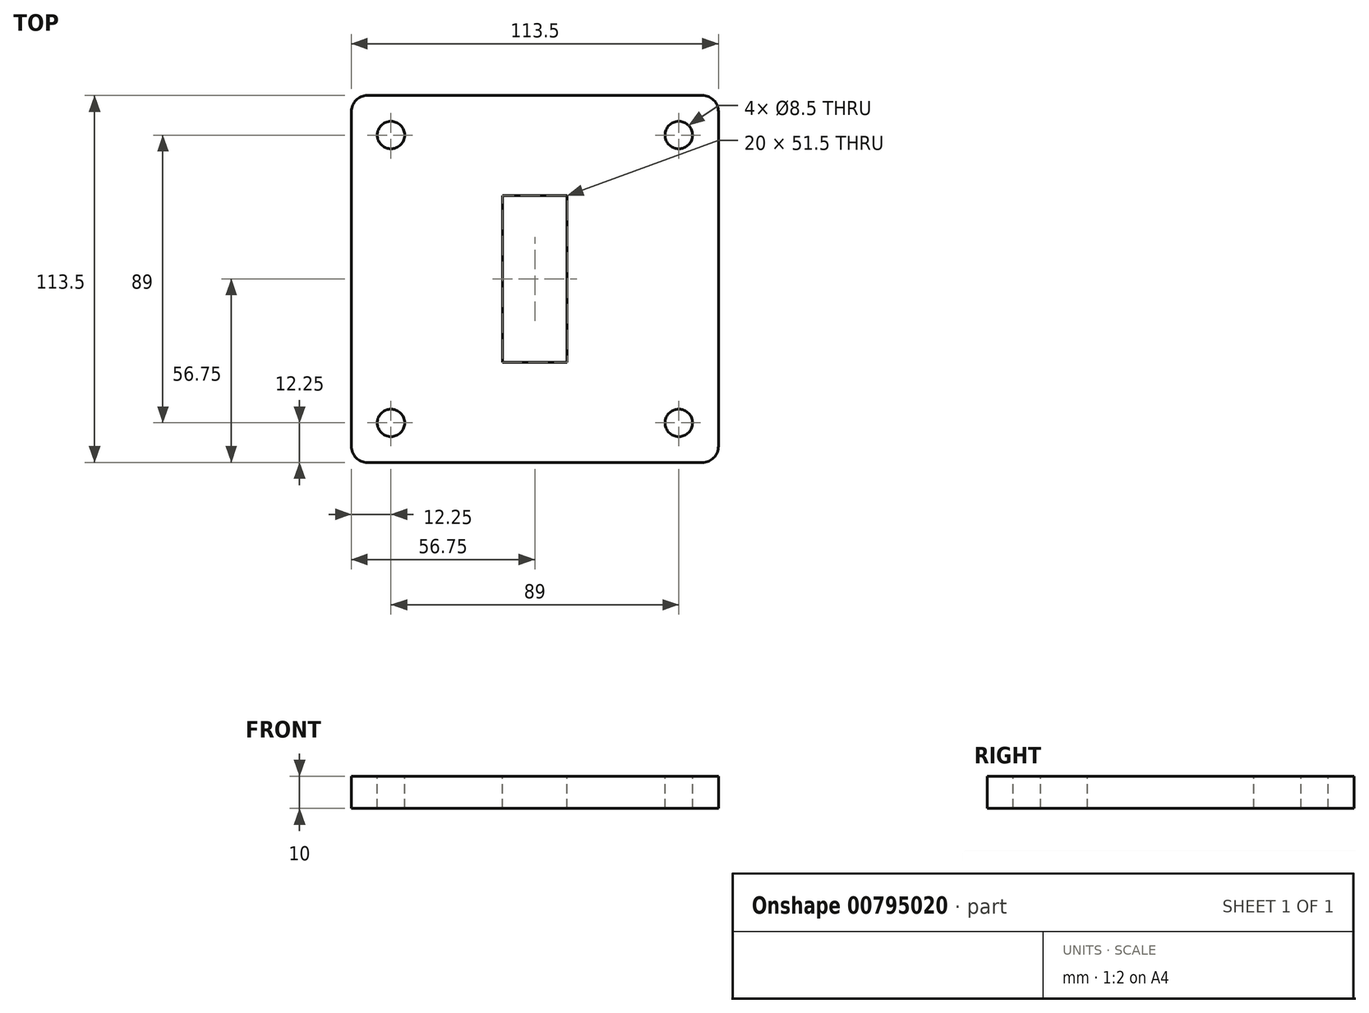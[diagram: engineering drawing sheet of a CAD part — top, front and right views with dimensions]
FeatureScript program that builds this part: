
annotation { "Feature Type Name" : "Feature", "Feature Type Description" : "" }
export const myFeature = defineFeature(function(context is Context, id is Id, definition is map)
    precondition{}
    {
        {
            var Q0;
            Q0=qCreatedBy(makeId("Top.planeOp"),FACE);
            var sketch = newSketch(context, id + "F0", { "sketchPlane" : qUnion([Q0])});
            skLineSegment(sketch, "E0.bottom", {"start": v(-56.75, 56.75) * mm, "end": v(56.75, 56.75) * mm});
            skLineSegment(sketch, "E0.top", {"start": v(-56.75, -56.75) * mm, "end": v(56.75, -56.75) * mm});
            skLineSegment(sketch, "E0.left", {"start": v(-56.75, 56.75) * mm, "end": v(-56.75, -56.75) * mm});
            skLineSegment(sketch, "E0.right", {"start": v(56.75, 56.75) * mm, "end": v(56.75, -56.75) * mm});
            skPoint(sketch, "E0.middle", {"position": v(0, 0) * mm});
            skSolve(sketch);
        }
        {
            var Q0;
            Q0=makeQuery(id+"F0.imprint","IMPRINT",FACE,{"disambiguationData":[TD([[makeQuery(id+"F0.imprint","IMPRINT",EDGE,{"derivedFrom":sQuery(id+"F0.wireOp",EDGE,"E0.bottom")}),-1.0]])]});
            extrude(context, id + "F1", {"entities" : qUnion([Q0]), "depth" : 10 * mm, "offsetDistance" : 25 * mm});
        }
        {
            var Q0;
            Q0=makeQuery(id+"F1.opExtrude","SWEPT_EDGE",EDGE,{"disambiguationData":[OSD([sQuery(id+"F0.wireOp",EDGE,"E0.top"),sQuery(id+"F0.wireOp",EDGE,"E0.left")])]});
            var Q1;
            Q1=makeQuery(id+"F1.opExtrude","SWEPT_EDGE",EDGE,{"disambiguationData":[OSD([sQuery(id+"F0.wireOp",EDGE,"E0.bottom"),sQuery(id+"F0.wireOp",EDGE,"E0.left")])]});
            var Q2;
            Q2=makeQuery(id+"F1.opExtrude","SWEPT_EDGE",EDGE,{"disambiguationData":[OSD([sQuery(id+"F0.wireOp",EDGE,"E0.bottom"),sQuery(id+"F0.wireOp",EDGE,"E0.right")])]});
            var Q3;
            Q3=makeQuery(id+"F1.opExtrude","SWEPT_EDGE",EDGE,{"disambiguationData":[OSD([sQuery(id+"F0.wireOp",EDGE,"E0.top"),sQuery(id+"F0.wireOp",EDGE,"E0.right")])]});
            fillet(context, id + "F2", {"entities" : qUnion([Q0, Q1, Q2, Q3]), "radius" : 5 * mm, "tangentPropagation" : true, "allowEdgeOverflow" : false});
        }
        {
            var Q0;
            Q0=makeQuery(id+"F1.opExtrude","CAP_FACE",FACE,{"disambiguationData":[OSD([sQuery(id+"F0.wireOp",EDGE,"E0.bottom"),sQuery(id+"F0.wireOp",EDGE,"E0.top"),sQuery(id+"F0.wireOp",EDGE,"E0.left"),sQuery(id+"F0.wireOp",EDGE,"E0.right")])],"isStart":false});
            var sketch = newSketch(context, id + "F3", { "sketchPlane" : qUnion([Q0])});
            skCircle(sketch, "E1", {"center": v(-44.5, -44.5) * mm, "radius": 4.25 * mm});
            skCircle(sketch, "E2", {"center": v(44.5, -44.5) * mm, "radius": 4.25 * mm});
            skCircle(sketch, "E3", {"center": v(-44.5, 44.5) * mm, "radius": 4.25 * mm});
            skCircle(sketch, "E4", {"center": v(44.5, 44.5) * mm, "radius": 4.25 * mm});
            skSolve(sketch);
        }
        {
            var Q0;
            Q0 = qSketchRegion(id + "F3", true);
            extrude(context, id + "F4", {"entities" : qUnion([Q0]), "operationType" : NewBodyOperationType.REMOVE, "oppositeDirection" : true, "depth" : 10 * mm, "offsetDistance" : 25 * mm});
        }
        {
            var Q0;
            Q0=makeQuery(id+"F1.opExtrude","CAP_FACE",FACE,{"disambiguationData":[OSD([sQuery(id+"F0.wireOp",EDGE,"E0.bottom"),sQuery(id+"F0.wireOp",EDGE,"E0.top"),sQuery(id+"F0.wireOp",EDGE,"E0.left"),sQuery(id+"F0.wireOp",EDGE,"E0.right")])],"isStart":false});
            var sketch = newSketch(context, id + "F5", { "sketchPlane" : qUnion([Q0])});
            skPoint(sketch, "E5.middle", {"position": v(0, 0) * mm});
            skLineSegment(sketch, "E6.bottom", {"start": v(-10, 25.75) * mm, "end": v(10, 25.75) * mm});
            skLineSegment(sketch, "E6.top", {"start": v(-10, -25.75) * mm, "end": v(10, -25.75) * mm});
            skLineSegment(sketch, "E6.left", {"start": v(-10, 25.75) * mm, "end": v(-10, -25.75) * mm});
            skLineSegment(sketch, "E6.right", {"start": v(10, 25.75) * mm, "end": v(10, -25.75) * mm});
            skSolve(sketch);
        }
        {
            var Q0;
            Q0=makeQuery(id+"F5.imprint","IMPRINT",FACE,{"disambiguationData":[TD([[makeQuery(id+"F5.imprint","IMPRINT",EDGE,{"derivedFrom":sQuery(id+"F5.wireOp",EDGE,"E6.bottom")}),-1.0]])]});
            extrude(context, id + "F6", {"entities" : qUnion([Q0]), "operationType" : NewBodyOperationType.REMOVE, "oppositeDirection" : true, "depth" : 10 * mm, "offsetDistance" : 25 * mm});
        }
    });
